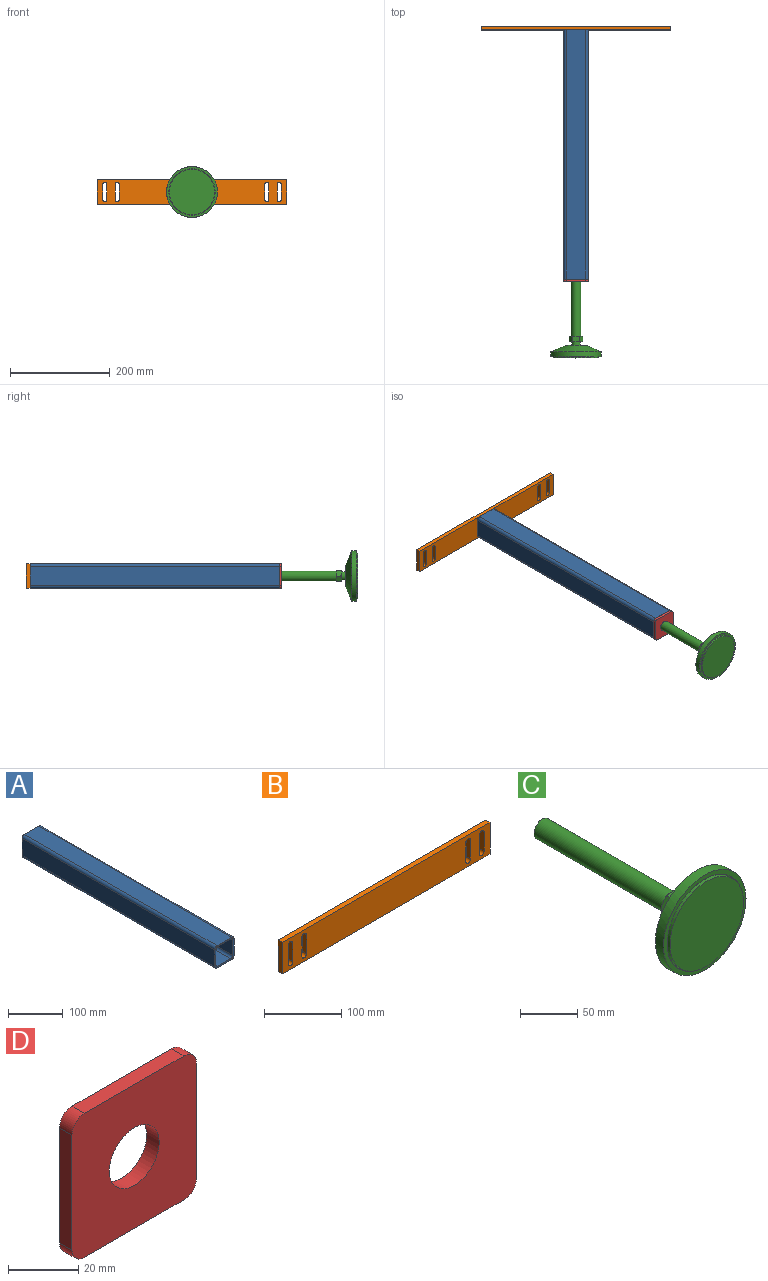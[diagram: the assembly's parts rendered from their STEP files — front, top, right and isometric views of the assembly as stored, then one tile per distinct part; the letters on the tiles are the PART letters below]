
ASSEMBLY  parts=4 mates=3
PART A: 18 faces, bbox 50x500x50 mm
  f0: plane 500x38mm, normal (0,0,-1), area 19000mm2, adj f4,f5,f14,f17
  f1: plane 500x38mm, normal (1,0,0), area 19000mm2, adj f4,f5,f14,f15
  f2: plane 500x38mm, normal (0,0,1), area 19000mm2, adj f4,f5,f15,f16
  f3: plane 500x38mm, normal (-1,0,0), area 19000mm2, adj f4,f5,f16,f17
  f4: plane 50x50mm, normal (0,-1,0), area 554.6mm2, adj f0,f1,f2,f3,f6,f7,f8,f9
  f5: plane 50x50mm, normal (0,1,0), area 554.6mm2, adj f0,f1,f2,f3,f6,f7,f8,f9
  f6: plane 500x34mm, normal (0,0,-1), area 17000mm2, adj f4,f5,f7,f13
  f7: cylinder r=5mm len=500mm, axis (0,-1,0), area 3927mm2, adj f4,f5,f6,f8
  f8: plane 500x34mm, normal (1,0,0), area 17000mm2, adj f4,f5,f7,f9
  f9: cylinder r=5mm len=500mm, axis (0,-1,0), area 3927mm2, adj f4,f5,f8,f10
  f10: plane 500x34mm, normal (0,0,1), area 17000mm2, adj f4,f5,f9,f11
  f11: cylinder r=5mm len=500mm, axis (0,-1,0), area 3927mm2, adj f4,f5,f10,f12
  f12: plane 500x34mm, normal (-1,0,0), area 17000mm2, adj f4,f5,f11,f13
  f13: cylinder r=5mm len=500mm, axis (0,-1,0), area 3927mm2, adj f4,f5,f6,f12
  f14: cylinder r=6mm len=500mm, axis (0,-1,0), area 4712.4mm2, adj f0,f1,f4,f5
  f15: cylinder r=6mm len=500mm, axis (0,1,0), area 4712.4mm2, adj f1,f2,f4,f5
  f16: cylinder r=6mm len=500mm, axis (0,-1,0), area 4712.4mm2, adj f2,f3,f4,f5
  f17: cylinder r=6mm len=500mm, axis (0,1,0), area 4712.4mm2, adj f0,f3,f4,f5
PART B: 22 faces, bbox 380x8x50 mm
  f0: plane 380x8mm, normal (0,0,-1), area 3040mm2, adj f1,f3,f4,f5
  f1: plane 50x8mm, normal (1,0,0), area 400mm2, adj f0,f2,f4,f5
  f2: plane 380x8mm, normal (0,0,1), area 3040mm2, adj f1,f3,f4,f5
  f3: plane 50x8mm, normal (-1,0,0), area 400mm2, adj f0,f2,f4,f5
  f4: plane 380x50mm, normal (0,-1,0), area 17753mm2, adj f0,f1,f2,f3,f6,f7,f8,f9
  f5: plane 380x50mm, normal (0,1,0), area 17753mm2, adj f0,f1,f2,f3,f6,f7,f8,f9
  f6: plane 30x8mm, normal (-1,0,0), area 240mm2, adj f4,f5,f7,f9
  f7: cylinder r=4.25mm len=8.5mm, axis (0,1,0), area 106.8mm2, adj f4,f5,f6,f8
  f8: plane 30x8mm, normal (1,0,0), area 240mm2, adj f4,f5,f7,f9
  f9: cylinder r=4.25mm len=8.5mm, axis (0,1,0), area 106.8mm2, adj f4,f5,f6,f8
  f10: plane 30x8mm, normal (-1,0,0), area 240mm2, adj f4,f5,f11,f13
  f11: cylinder r=4.25mm len=8.5mm, axis (0,1,0), area 106.8mm2, adj f4,f5,f10,f12
  f12: plane 30x8mm, normal (1,0,0), area 240mm2, adj f4,f5,f11,f13
  f13: cylinder r=4.25mm len=8.5mm, axis (0,1,0), area 106.8mm2, adj f4,f5,f10,f12
  f14: plane 30x8mm, normal (-1,0,0), area 240mm2, adj f4,f5,f15,f17
  f15: cylinder r=4.25mm len=8.5mm, axis (0,1,0), area 106.8mm2, adj f4,f5,f14,f16
  f16: plane 30x8mm, normal (1,0,0), area 240mm2, adj f4,f5,f15,f17
  f17: cylinder r=4.25mm len=8.5mm, axis (0,1,0), area 106.8mm2, adj f4,f5,f14,f16
  f18: plane 30x8mm, normal (-1,0,0), area 240mm2, adj f4,f5,f19,f21
  f19: cylinder r=4.25mm len=8.5mm, axis (0,1,0), area 106.8mm2, adj f4,f5,f18,f20
  f20: plane 30x8mm, normal (1,0,0), area 240mm2, adj f4,f5,f19,f21
  f21: cylinder r=4.25mm len=8.5mm, axis (0,1,0), area 106.8mm2, adj f4,f5,f18,f20
PART C: 31 faces, bbox 103.2x204.7x103.2 mm
  f0: plane 15.1x11.72mm, normal (0,0,-1), area 141.6mm2, adj f1,f2,f7,f8,f9,f27,f28,f30
  f1: torus R=12.38mm, axis (0,1,0), area 8.7mm2, adj f0,f2,f9
  f2: plane 13.24x11.72mm, normal (0.87,0,-0.5), area 141.1mm2, adj f0,f1,f5,f7,f9,f10,f26,f27
  f3: torus R=12.38mm, axis (0,1,0), area 8.7mm2, adj f5,f6,f7
  f4: plane 13.24x11.72mm, normal (-0.87,0,0.5), area 141.4mm2, adj f6,f7,f8,f9,f12,f13,f25,f29
  f5: plane 13.24x11.72mm, normal (0.87,0,0.5), area 141.5mm2, adj f2,f3,f6,f7,f9,f10,f11,f26
  f6: plane 15.1x11.72mm, normal (0,0,1), area 141.5mm2, adj f3,f4,f5,f7,f9,f11,f12,f25
  f7: plane 24.75x24.03mm, normal (0,1,0), area 158.4mm2, adj f0,f2,f3,f4,f5,f6,f8,f14
  f8: plane 13.24x11.72mm, normal (-0.87,0,-0.5), area 141.4mm2, adj f0,f4,f7,f9,f13,f28,f29,f30
  f9: plane 24.75x24.03mm, normal (0,-1,0), area 245.6mm2, adj f0,f1,f2,f4,f5,f6,f8,f10
  f10: torus R=12.38mm, axis (0,1,0), area 8.7mm2, adj f2,f5,f9
  f11: torus R=12.38mm, axis (0,1,0), area 8.7mm2, adj f5,f6,f9
  f12: torus R=12.38mm, axis (0,1,0), area 8.7mm2, adj f4,f6,f9
  f13: torus R=12.38mm, axis (0,1,0), area 8.7mm2, adj f4,f8,f9
  f14: cylinder r=10mm len=160mm, axis (0,-1,0), area 10053.1mm2, adj f7,f15
  f15: plane 20x20mm, normal (0,1,0), area 314.2mm2, adj f14
  f16: plane 42x42mm, normal (0,1,0), area 1158.5mm2, adj f19,f24
  f17: plane 91x91mm, normal (0,-1,0), area 6503.9mm2, adj f20
  f18: cylinder r=51mm len=102mm, axis (0,-1,0), area 3204.4mm2, adj f19,f21
  f19: cone r=21mm half-angle=67.4deg, axis (0,-1,0), area 7351.3mm2, adj f16,f18
  f20: cylinder r=45.5mm len=91mm, axis (0,-1,0), area 1000.6mm2, adj f17,f23
  f21: plane 102x102mm, normal (0,-1,0), area 1378.4mm2, adj f18,f22
  f22: cylinder r=46.5mm len=93mm, axis (0,-1,0), area 292.2mm2, adj f21,f23
  f23: plane 93x93mm, normal (0,-1,0), area 289mm2, adj f20,f22
  f24: cylinder r=8.5mm len=17mm, axis (0,-1,0), area 427.3mm2, adj f9,f16
  f25: torus R=12.38mm, axis (0,1,0), area 8.7mm2, adj f4,f6,f7
  f26: torus R=12.38mm, axis (0,1,0), area 8.7mm2, adj f2,f5,f7
  f27: torus R=12.38mm, axis (0,1,0), area 8.7mm2, adj f0,f2,f7
  f28: torus R=12.38mm, axis (0,1,0), area 8.7mm2, adj f0,f7,f8
  f29: torus R=12.38mm, axis (0,1,0), area 8.7mm2, adj f4,f7,f8
  f30: torus R=12.38mm, axis (0,1,0), area 8.7mm2, adj f0,f8,f9
PART D: 11 faces, bbox 50x5x50 mm
  f0: plane 40x5mm, normal (0,0,-1), area 200mm2, adj f4,f5,f6,f9
  f1: plane 40x5mm, normal (1,0,0), area 200mm2, adj f4,f5,f6,f7
  f2: plane 40x5mm, normal (0,0,1), area 200mm2, adj f4,f5,f7,f8
  f3: plane 40x5mm, normal (-1,0,0), area 200mm2, adj f4,f5,f8,f9
  f4: plane 50x50mm, normal (0,-1,0), area 2164.4mm2, adj f0,f1,f2,f3,f6,f7,f8,f9
  f5: plane 50x50mm, normal (0,1,0), area 2164.4mm2, adj f0,f1,f2,f3,f6,f7,f8,f9
  f6: cylinder r=5mm len=5mm, axis (0,-1,0), area 39.3mm2, adj f0,f1,f4,f5
  f7: cylinder r=5mm len=5mm, axis (0,1,0), area 39.3mm2, adj f1,f2,f4,f5
  f8: cylinder r=5mm len=5mm, axis (0,-1,0), area 39.3mm2, adj f2,f3,f4,f5
  f9: cylinder r=5mm len=5mm, axis (0,1,0), area 39.3mm2, adj f0,f3,f4,f5
  f10: cylinder r=10mm len=20mm, axis (0,-1,0), area 314.2mm2, adj f4,f5
PLACE A t=(-97.54,168.4,-37.93)mm
PLACE B t=(-97.54,176.4,-37.93)mm
PLACE C t=(-97.54,-490.1,-37.93)mm
PLACE D t=(-97.54,-331.6,-37.93)mm
MATE fastened C.f14 <-> D.f10  axis (0,-1,0) through (-97.54,-286.6,-37.93)mm
MATE fastened D.f5 <-> A.f4  axis (0,1,0) through (-97.54,-331.6,-12.93)mm
MATE fastened B.f4 <-> A.f5  axis (0,-1,0) through (-97.54,168.4,-37.93)mm
